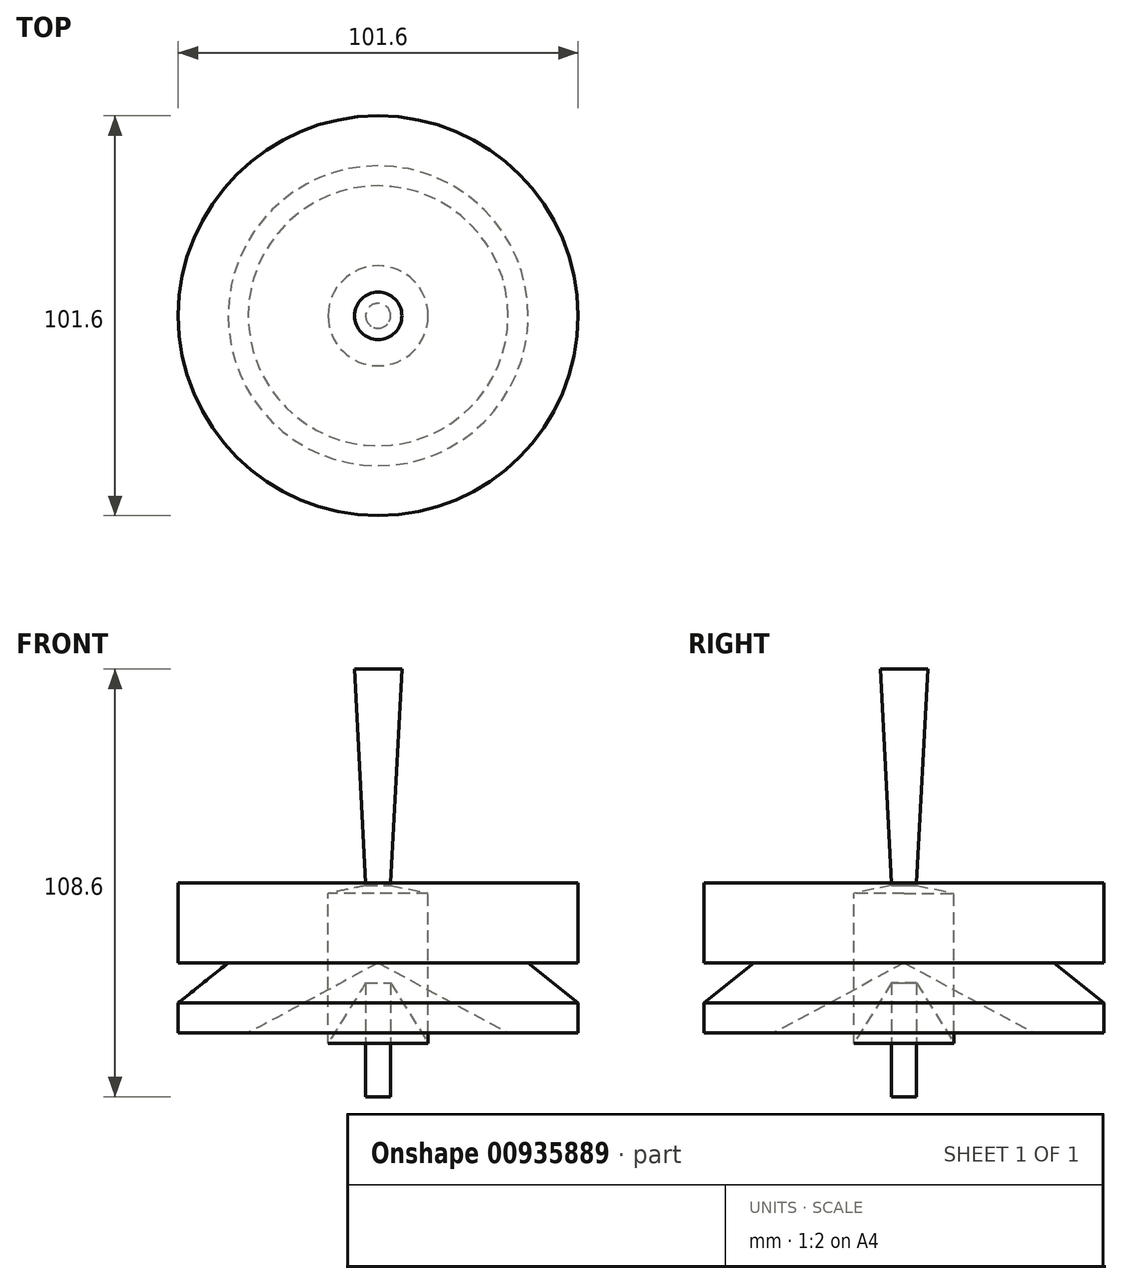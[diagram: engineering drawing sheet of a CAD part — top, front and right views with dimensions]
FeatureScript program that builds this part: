
annotation { "Feature Type Name" : "Feature", "Feature Type Description" : "" }
export const myFeature = defineFeature(function(context is Context, id is Id, definition is map)
    precondition{}
    {
        {
            var Q0;
            Q0=qCreatedBy(makeId("Right.planeOp"),FACE);
            var sketch = newSketch(context, id + "F0", { "sketchPlane" : qUnion([Q0])});
            skLineSegment(sketch, "E0", {"start": v(12.7, -2.6) * mm, "end": v(0, 0) * mm});
            skLineSegment(sketch, "E1", {"start": v(12.7, -2.6) * mm, "end": v(12.7, -40.7) * mm});
            skLineSegment(sketch, "E2", {"start": v(12.7, -40.7) * mm, "end": v(0, -20.32) * mm});
            skLineSegment(sketch, "E3", {"start": v(0, 0) * mm, "end": v(0, -20.32) * mm});
            skSolve(sketch);
        }
        {
            var Q0;
            Q0=qCreatedBy(makeId("Right.planeOp"),FACE);
            var sketch = newSketch(context, id + "F1", { "sketchPlane" : qUnion([Q0])});
            skLineSegment(sketch, "E4", {"start": v(0, 76.79) * mm, "end": v(0, -75.61) * mm});
            skSolve(sketch);
        }
        {
            var Q0;
            Q0 = qSketchRegion(id + "F0", true);
            var Q1;
            Q1=sQuery(id+"F1.wireOp",EDGE,"E4");
            revolve(context, id + "F2", {"surfaceOperationType" : NewSurfaceOperationType.NEW, "entities" : qUnion([Q0]), "axis" : qUnion([Q1]), "revolveType" : RevolveType.FULL});
        }
        {
            var Q0;
            Q0=qCreatedBy(makeId("Top.planeOp"),FACE);
            var sketch = newSketch(context, id + "F3", { "sketchPlane" : qUnion([Q0])});
            skCircle(sketch, "E5", {"center": v(0, 0) * mm, "radius": 3.18 * mm});
            skSolve(sketch);
        }
        {
            var Q0;
            Q0 = qSketchRegion(id + "F3", true);
            extrude(context, id + "F4", {"entities" : qUnion([Q0]), "operationType" : NewBodyOperationType.ADD, "endBound" : BoundingType.THROUGH_ALL, "depth" : 25.4 * mm, "offsetDistance" : 25.4 * mm, "hasDraft" : true, "draftAngle" : 3 * degree, "hasSecondDirection" : true, "secondDirectionBound" : SecondDirectionBoundingType.THROUGH_ALL, "secondDirectionOppositeDirection" : true, "secondDirectionDepth" : 127 * mm});
        }
        {
            var Q0;
            Q0=qCreatedBy(makeId("Front.planeOp"),FACE);
            var sketch = newSketch(context, id + "F5", { "sketchPlane" : qUnion([Q0])});
            skLineSegment(sketch, "E6", {"start": v(0, 0) * mm, "end": v(-50.8, 0) * mm});
            skLineSegment(sketch, "E7", {"start": v(-50.8, 0) * mm, "end": v(-50.8, -20.32) * mm});
            skLineSegment(sketch, "E8", {"start": v(-50.8, -20.32) * mm, "end": v(-38.1, -20.32) * mm});
            skLineSegment(sketch, "E9", {"start": v(-38.1, -20.32) * mm, "end": v(-50.8, -30.48) * mm});
            skLineSegment(sketch, "E10", {"start": v(-50.8, -30.48) * mm, "end": v(-50.8, -38.1) * mm});
            skLineSegment(sketch, "E11", {"start": v(-50.8, -38.1) * mm, "end": v(-33.02, -38.1) * mm});
            skLineSegment(sketch, "E12", {"start": v(-33.02, -38.1) * mm, "end": v(0, -20.32) * mm});
            skLineSegment(sketch, "E13", {"start": v(0, -20.32) * mm, "end": v(0, 0) * mm});
            skSolve(sketch);
        }
        {
            var Q0;
            Q0=makeQuery(id+"F5.imprint","IMPRINT",FACE,{"disambiguationData":[TD([[makeQuery(id+"F5.imprint","IMPRINT",EDGE,{"derivedFrom":sQuery(id+"F5.wireOp",EDGE,"E6")}),1.0]])]});
            var Q1;
            Q1=sQuery(id+"F5.wireOp",EDGE,"E13");
            revolve(context, id + "F6", {"surfaceOperationType" : NewSurfaceOperationType.NEW, "entities" : qUnion([Q0]), "axis" : qUnion([Q1]), "revolveType" : RevolveType.FULL});
        }
    });
